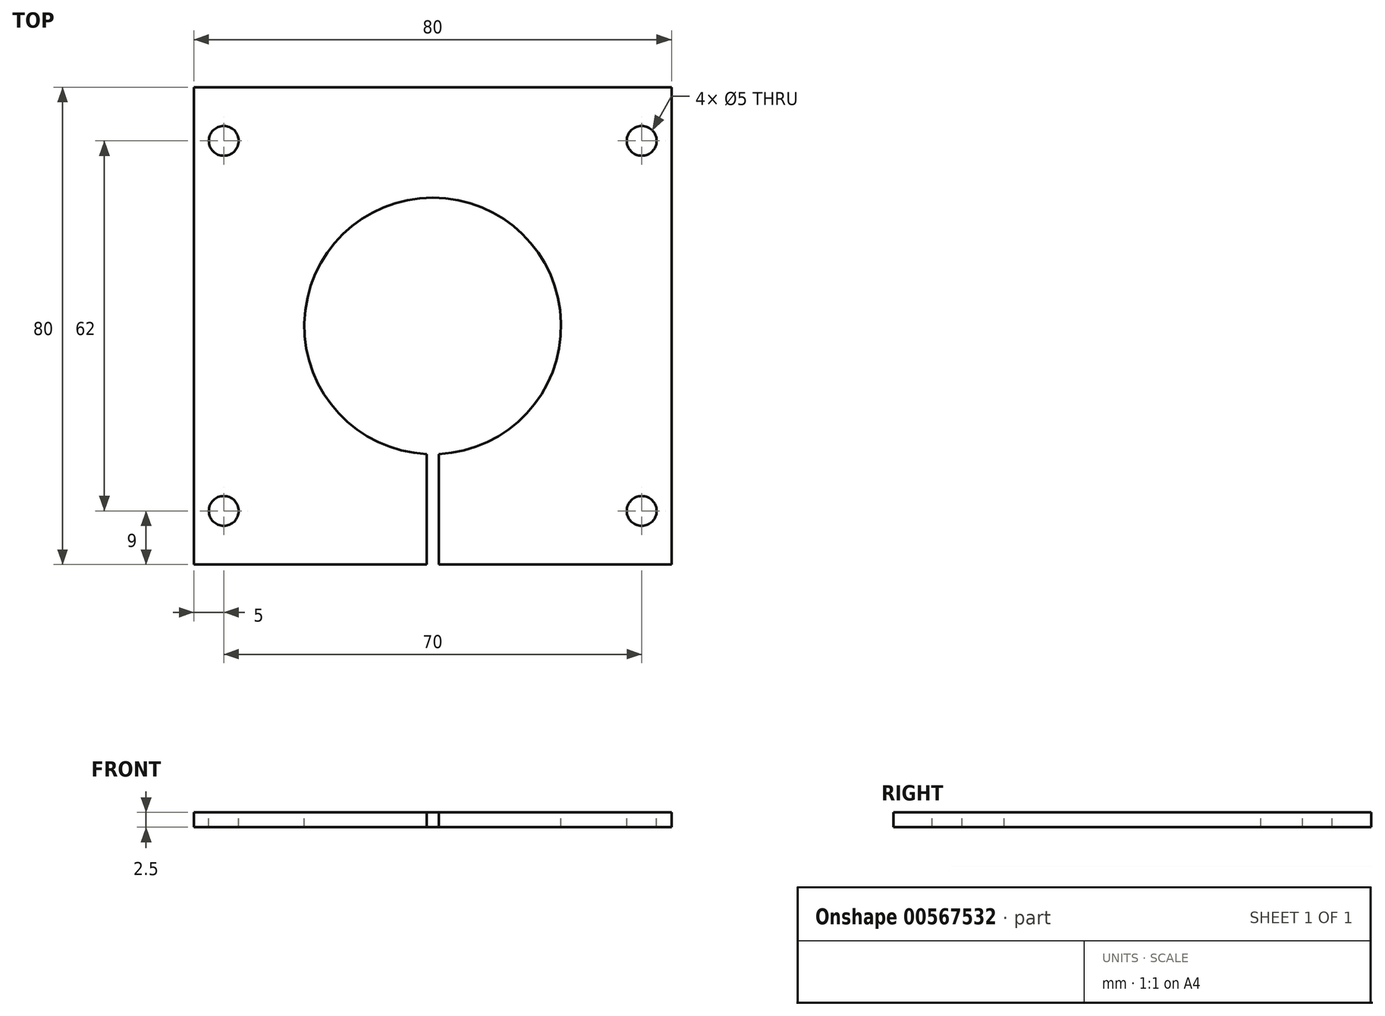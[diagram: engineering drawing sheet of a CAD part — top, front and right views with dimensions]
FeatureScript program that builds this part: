
annotation { "Feature Type Name" : "Feature", "Feature Type Description" : "" }
export const myFeature = defineFeature(function(context is Context, id is Id, definition is map)
    precondition{}
    {
        {
            var Q0;
            Q0=qCreatedBy(makeId("Top.planeOp"),FACE);
            var sketch = newSketch(context, id + "F0", { "sketchPlane" : qUnion([Q0])});
            skLineSegment(sketch, "E0.bottom", {"start": v(40, 40) * mm, "end": v(-40, 40) * mm});
            skLineSegment(sketch, "E0.top", {"start": v(40, -40) * mm, "end": v(-40, -40) * mm});
            skLineSegment(sketch, "E0.left", {"start": v(40, 40) * mm, "end": v(40, -40) * mm});
            skLineSegment(sketch, "E0.right", {"start": v(-40, 40) * mm, "end": v(-40, -40) * mm});
            skPoint(sketch, "E0.middle", {"position": v(0, 0) * mm});
            skCircle(sketch, "E1", {"center": v(35, 31) * mm, "radius": 2.5 * mm});
            skCircle(sketch, "E2", {"center": v(-35, 31) * mm, "radius": 2.5 * mm});
            skCircle(sketch, "E3", {"center": v(-35, -31) * mm, "radius": 2.5 * mm});
            skCircle(sketch, "E4", {"center": v(35, -31) * mm, "radius": 2.5 * mm});
            skCircle(sketch, "E5", {"center": v(0, 0) * mm, "radius": 21.5 * mm});
            skLineSegment(sketch, "E6", {"start": v(0, -40) * mm, "end": v(0, -21.5) * mm});
            skLineSegment(sketch, "E7.bottom", {"start": v(1, -21.5) * mm, "end": v(-1, -21.5) * mm});
            skLineSegment(sketch, "E7.top", {"start": v(1, -40) * mm, "end": v(-1, -40) * mm});
            skLineSegment(sketch, "E7.left", {"start": v(1, -21.48) * mm, "end": v(1, -40) * mm});
            skLineSegment(sketch, "E7.right", {"start": v(-1, -21.5) * mm, "end": v(-1, -40) * mm});
            skPoint(sketch, "E7.middle", {"position": v(0, -30.75) * mm});
            skLineSegment(sketch, "E8", {"start": v(-1, -21.48) * mm, "end": v(-1, -40) * mm});
            skLineSegment(sketch, "E9", {"start": v(1, -21.5) * mm, "end": v(1, -40) * mm});
            skSolve(sketch);
        }
        {
            var Q0;
            Q0=makeQuery(id+"F0.imprint","IMPRINT",FACE,{"disambiguationData":[TD([[makeQuery(id+"F0.imprint","IMPRINT",EDGE,{"derivedFrom":sQuery(id+"F0.wireOp",EDGE,"E0.bottom")}),1.0]])]});
            extrude(context, id + "F1", {"entities" : qUnion([Q0]), "endBound" : BoundingType.SYMMETRIC, "oppositeDirection" : true, "depth" : 2.5 * mm, "offsetDistance" : 25 * mm});
        }
    });
